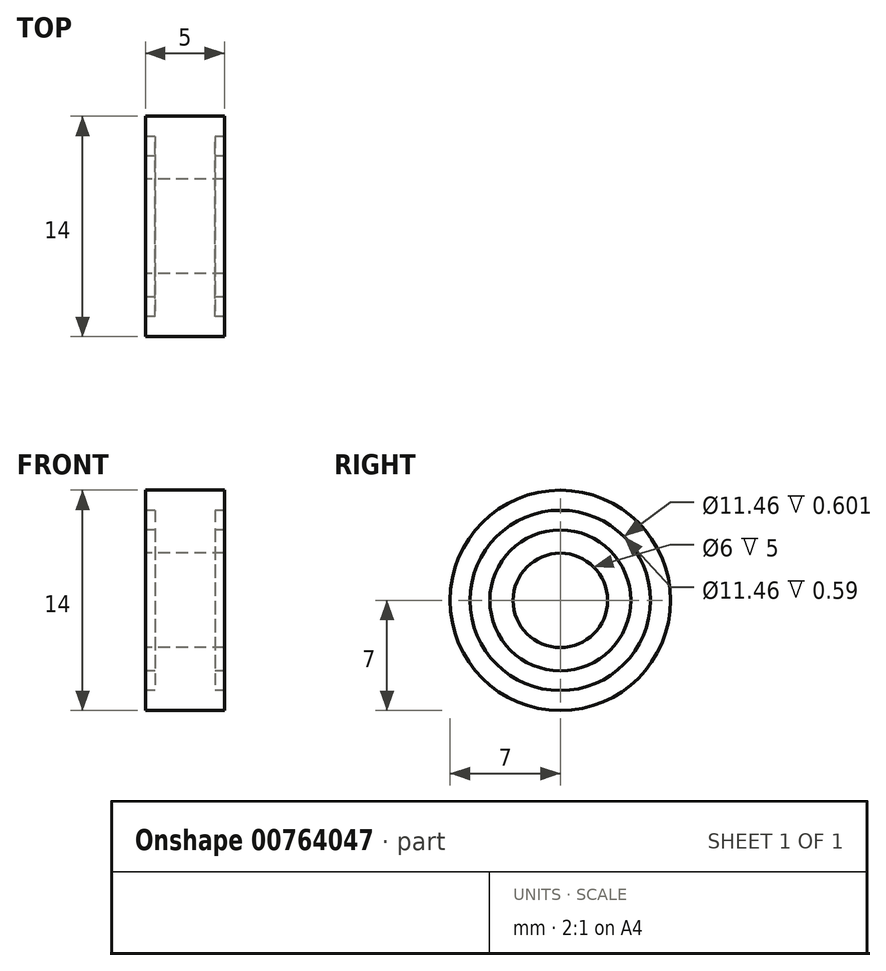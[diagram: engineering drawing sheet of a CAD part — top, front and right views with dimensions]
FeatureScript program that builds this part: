
annotation { "Feature Type Name" : "Feature", "Feature Type Description" : "" }
export const myFeature = defineFeature(function(context is Context, id is Id, definition is map)
    precondition{}
    {
        {
            var Q0;
            Q0=qCreatedBy(makeId("Front.planeOp"),FACE);
            var sketch = newSketch(context, id + "F0", { "sketchPlane" : qUnion([Q0])});
            skLineSegment(sketch, "E0.bottom", {"start": v(0, 7) * mm, "end": v(5, 7) * mm});
            skLineSegment(sketch, "E0.top", {"start": v(0, 3) * mm, "end": v(5, 3) * mm});
            skLineSegment(sketch, "E0.left", {"start": v(0, 7) * mm, "end": v(0, 5.73) * mm});
            skLineSegment(sketch, "E0.right", {"start": v(5, 7) * mm, "end": v(5, 5.73) * mm});
            skLineSegment(sketch, "E1.bottom", {"start": v(5, 5.73) * mm, "end": v(4.4, 5.73) * mm});
            skLineSegment(sketch, "E1.top", {"start": v(5, 4.47) * mm, "end": v(4.4, 4.47) * mm});
            skLineSegment(sketch, "E1.right", {"start": v(4.4, 5.73) * mm, "end": v(4.4, 4.47) * mm});
            skLineSegment(sketch, "E2.bottom", {"start": v(0, 5.73) * mm, "end": v(0.6, 5.73) * mm});
            skLineSegment(sketch, "E2.top", {"start": v(0, 4.47) * mm, "end": v(0.6, 4.47) * mm});
            skLineSegment(sketch, "E2.right", {"start": v(0.6, 5.73) * mm, "end": v(0.6, 4.47) * mm});
            skLineSegment(sketch, "E3.trimOffspring", {"start": v(5, 4.47) * mm, "end": v(5, 3) * mm});
            skLineSegment(sketch, "E4.trimOffspring", {"start": v(0, 4.47) * mm, "end": v(0, 3) * mm});
            skLineSegment(sketch, "E5", {"start": v(0, 0) * mm, "end": v(4.43, 0) * mm, "construction": true});
            skSolve(sketch);
        }
        {
            var Q0;
            Q0=makeQuery(id+"F0.imprint","IMPRINT",FACE,{"disambiguationData":[TD([[makeQuery(id+"F0.imprint","IMPRINT",EDGE,{"derivedFrom":sQuery(id+"F0.wireOp",EDGE,"E0.bottom")}),-1.0]])]});
            var Q1;
            Q1=sQuery(id+"F0.wireOp",EDGE,"E5");
            revolve(context, id + "F1", {"surfaceOperationType" : NewSurfaceOperationType.NEW, "entities" : qUnion([Q0]), "axis" : qUnion([Q1]), "revolveType" : RevolveType.FULL});
        }
    });
